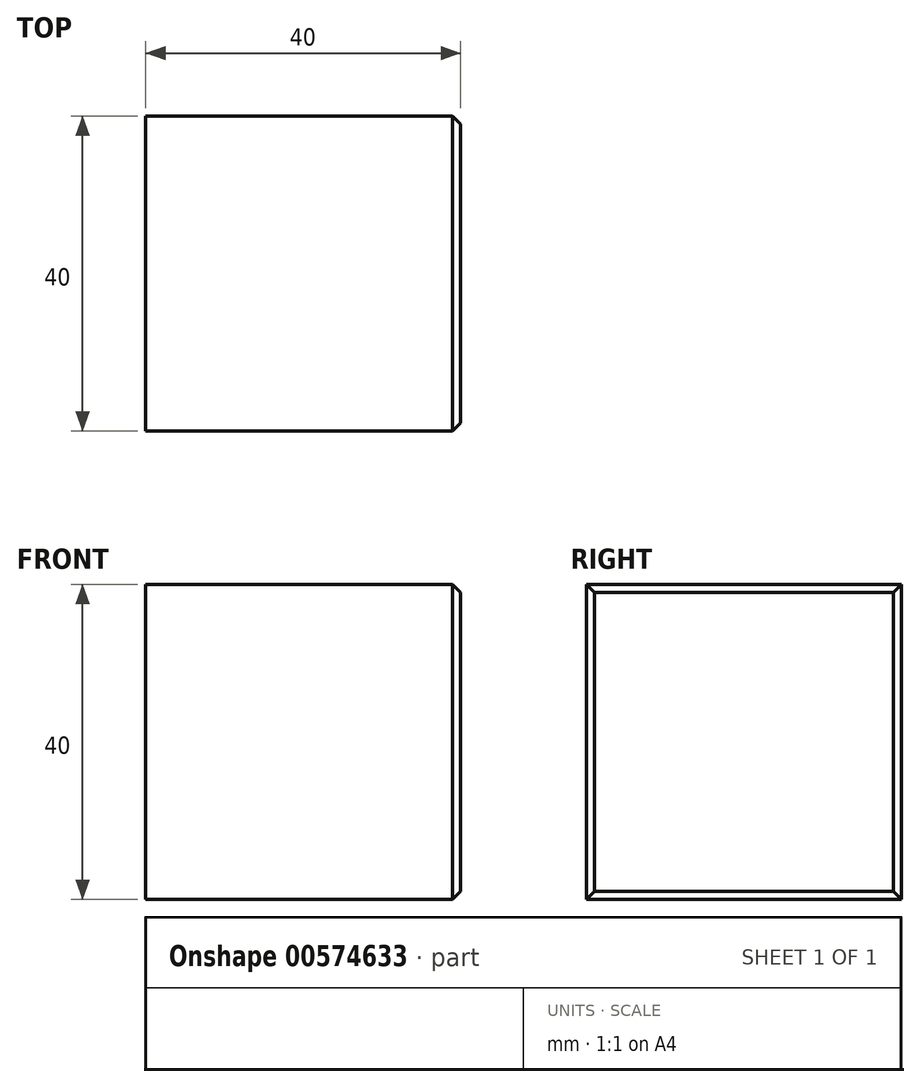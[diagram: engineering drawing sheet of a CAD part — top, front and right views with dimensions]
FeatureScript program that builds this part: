
annotation { "Feature Type Name" : "Feature", "Feature Type Description" : "" }
export const myFeature = defineFeature(function(context is Context, id is Id, definition is map)
    precondition{}
    {
        {
            var Q0;
            Q0=qCreatedBy(makeId("Top.planeOp"),FACE);
            var sketch = newSketch(context, id + "F0", { "sketchPlane" : qUnion([Q0])});
            skLineSegment(sketch, "E0.bottom", {"start": v(0, 0) * mm, "end": v(40, 0) * mm});
            skLineSegment(sketch, "E0.top", {"start": v(0, 40) * mm, "end": v(40, 40) * mm});
            skLineSegment(sketch, "E0.left", {"start": v(0, 0) * mm, "end": v(0, 40) * mm});
            skLineSegment(sketch, "E0.right", {"start": v(40, 0) * mm, "end": v(40, 40) * mm});
            skSolve(sketch);
        }
        {
            var Q0;
            Q0 = qSketchRegion(id + "F0", true);
            extrude(context, id + "F1", {"entities" : qUnion([Q0]), "depth" : 40 * mm, "offsetDistance" : 25 * mm});
        }
        {
            var Q0;
            Q0=makeQuery(id+"F1.opExtrude","SWEPT_FACE",FACE,{"disambiguationData":[OSD([sQuery(id+"F0.wireOp",EDGE,"E0.right")])]});
            chamfer(context, id + "F2", {"entities" : qUnion([Q0]), "width" : 1 * mm, "tangentPropagation" : true});
        }
    });
